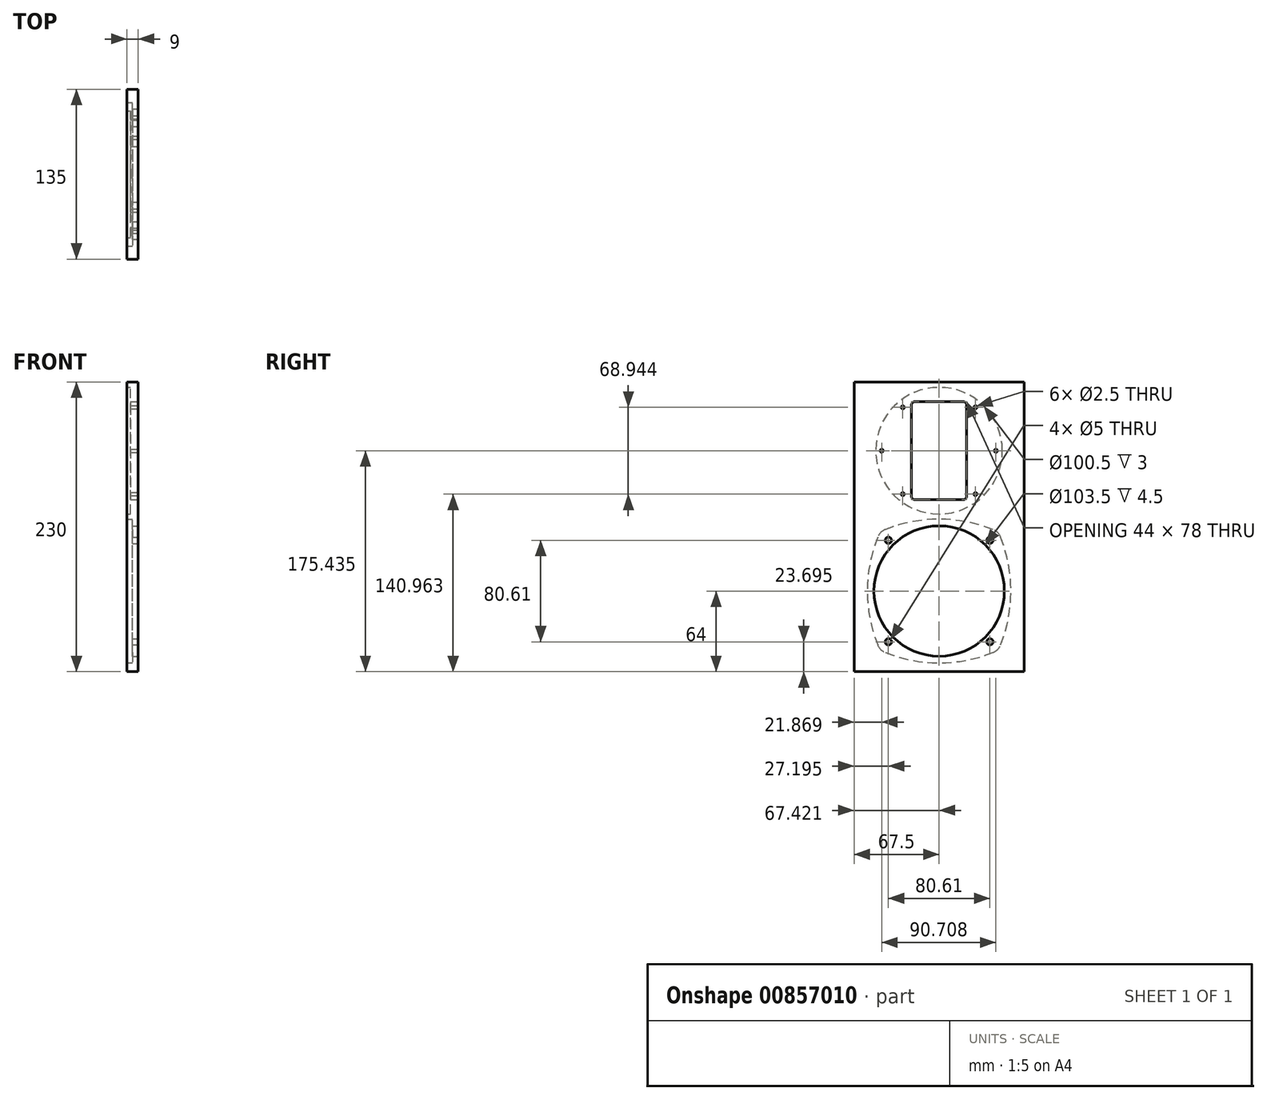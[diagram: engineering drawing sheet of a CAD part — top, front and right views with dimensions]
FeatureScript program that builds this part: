
annotation { "Feature Type Name" : "Feature", "Feature Type Description" : "" }
export const myFeature = defineFeature(function(context is Context, id is Id, definition is map)
    precondition{}
    {
        {
            var Q0;
            Q0=qCreatedBy(makeId("Right.planeOp"),FACE);
            var sketch = newSketch(context, id + "F0", { "sketchPlane" : qUnion([Q0])});
            skLineSegment(sketch, "E0.bottom", {"start": v(67.5, 115) * mm, "end": v(-67.5, 115) * mm});
            skLineSegment(sketch, "E0.left", {"start": v(67.5, 115) * mm, "end": v(67.5, -115) * mm});
            skLineSegment(sketch, "E0.right", {"start": v(-67.5, 115) * mm, "end": v(-67.5, -115) * mm});
            skLineSegment(sketch, "E1", {"start": v(67.5, -115) * mm, "end": v(-67.5, -115) * mm});
            skPoint(sketch, "E2", {"position": v(0, -51) * mm});
            skCircle(sketch, "E3", {"center": v(0, -51) * mm, "radius": 51.75 * mm});
            skCircle(sketch, "E4", {"center": v(40.3, -10.7) * mm, "radius": 2.5 * mm});
            skPoint(sketch, "E5", {"position": v(46.32, -4.68) * mm});
            skPoint(sketch, "E6", {"position": v(47.02, -3.98) * mm});
            skCircle(sketch, "E7.1.0", {"center": v(-40.3, -10.7) * mm, "radius": 2.5 * mm});
            skPoint(sketch, "E7.1.1", {"position": v(-46.32, -4.68) * mm});
            skPoint(sketch, "E7.1.2", {"position": v(-47.02, -3.98) * mm});
            skCircle(sketch, "E7.2.0", {"center": v(-40.3, -91.3) * mm, "radius": 2.5 * mm});
            skPoint(sketch, "E7.2.1", {"position": v(-46.32, -97.32) * mm});
            skPoint(sketch, "E7.2.2", {"position": v(-47.02, -98.02) * mm});
            skCircle(sketch, "E7.3.0", {"center": v(40.3, -91.3) * mm, "radius": 2.5 * mm});
            skPoint(sketch, "E7.3.1", {"position": v(46.32, -97.32) * mm});
            skPoint(sketch, "E7.3.2", {"position": v(47.02, -98.02) * mm});
            skPoint(sketch, "E8.1.0", {"position": v(-57, -51) * mm});
            skPoint(sketch, "E8.2.0", {"position": v(0, -108) * mm});
            skPoint(sketch, "E8.3.0", {"position": v(57, -51) * mm});
            skArc(sketch, "E9", {"start": v(47.02, -3.98) * mm, "mid": v(0, 6) * mm, "end": v(-47.02, -3.98) * mm});
            skArc(sketch, "E10", {"start": v(-47.02, -3.98) * mm, "mid": v(-57, -51) * mm, "end": v(-47.02, -98.02) * mm});
            skArc(sketch, "E11", {"start": v(-47.02, -98.02) * mm, "mid": v(0, -108) * mm, "end": v(47.02, -98.02) * mm});
            skArc(sketch, "E12", {"start": v(47.02, -98.02) * mm, "mid": v(57, -51) * mm, "end": v(47.02, -3.98) * mm});
            skLineSegment(sketch, "E13.trimOffspring", {"start": v(0, 6) * mm, "end": v(0, 115) * mm});
            skLineSegment(sketch, "E14.trimOffspring", {"start": v(46.32, -4.68) * mm, "end": v(47.02, -3.98) * mm});
            skPoint(sketch, "E15.start.orphan", {"position": v(0, -115) * mm});
            skCircle(sketch, "E16", {"center": v(-0.08, 60.44) * mm, "radius": 50.25 * mm});
            skCircle(sketch, "E17.3.0", {"center": v(28.85, 25.96) * mm, "radius": 1.25 * mm});
            skPoint(sketch, "E18", {"position": v(-193.88, 39.27) * mm});
            skLineSegment(sketch, "E19.bottom", {"start": v(-19.08, 99.44) * mm, "end": v(18.92, 99.44) * mm});
            skLineSegment(sketch, "E19.top", {"start": v(-19.08, 21.44) * mm, "end": v(18.92, 21.44) * mm});
            skLineSegment(sketch, "E19.left", {"start": v(-22.08, 96.44) * mm, "end": v(-22.08, 24.44) * mm});
            skLineSegment(sketch, "E19.right", {"start": v(21.92, 96.44) * mm, "end": v(21.92, 24.44) * mm});
            skPoint(sketch, "E20.visualSharp", {"position": v(21.92, 99.44) * mm});
            skArc(sketch, "E20.filletArc", {"start": v(21.92, 96.44) * mm, "mid": v(21.04, 98.56) * mm, "end": v(18.92, 99.44) * mm});
            skPoint(sketch, "E21.visualSharp", {"position": v(-22.08, 99.44) * mm});
            skArc(sketch, "E21.filletArc", {"start": v(-19.08, 99.44) * mm, "mid": v(-21.2, 98.56) * mm, "end": v(-22.08, 96.44) * mm});
            skPoint(sketch, "E22.visualSharp", {"position": v(-22.08, 21.44) * mm});
            skArc(sketch, "E22.filletArc", {"start": v(-22.08, 24.44) * mm, "mid": v(-21.2, 22.31) * mm, "end": v(-19.08, 21.44) * mm});
            skPoint(sketch, "E23.visualSharp", {"position": v(21.92, 21.44) * mm});
            skArc(sketch, "E23.filletArc", {"start": v(18.92, 21.44) * mm, "mid": v(21.04, 22.31) * mm, "end": v(21.92, 24.44) * mm});
            skLineSegment(sketch, "E24", {"start": v(-0.08, 60.44) * mm, "end": v(0, 60.44) * mm});
            skPoint(sketch, "E24.endSnap0", {"position": v(21.92, 60.44) * mm});
            skLineSegment(sketch, "E25", {"start": v(-0.08, 60.44) * mm, "end": v(0, 60.51) * mm});
            skLineSegment(sketch, "E26", {"start": v(-0.08, 60.44) * mm, "end": v(0, 60.34) * mm});
            skCircle(sketch, "E27.MirrorC", {"center": v(-28.85, 25.96) * mm, "radius": 1.25 * mm});
            skCircle(sketch, "E28.MirrorC", {"center": v(-28.85, 94.9) * mm, "radius": 1.25 * mm});
            skCircle(sketch, "E29.MirrorC", {"center": v(28.85, 94.9) * mm, "radius": 1.25 * mm});
            skCircle(sketch, "E30.3.0", {"center": v(45.08, 60.37) * mm, "radius": 1.25 * mm});
            skCircle(sketch, "E31.3.0", {"center": v(-45.63, 60.37) * mm, "radius": 1.25 * mm});
            skPoint(sketch, "E32.trimOffspring.end.orphan", {"position": v(44.92, 60.44) * mm});
            skSolve(sketch);
        }
        {
            var Q0;
            {var subQ4=sQuery(id+"F0.wireOp",EDGE,"E0.left");Q0=makeQuery(id+"F0.imprint","IMPRINT",FACE,{"disambiguationData":[TD([[makeQuery(id+"F0.imprint","IMPRINT",EDGE,{"derivedFrom":subQ4}),-1.0]])]});}
            extrude(context, id + "F1", {"entities" : qUnion([Q0]), "oppositeDirection" : true, "depth" : 9 * mm, "offsetDistance" : 25 * mm});
        }
        {
            var Q0;
            Q0=makeQuery(id+"F0.imprint","IMPRINT",FACE,{"disambiguationData":[TD([[makeQuery(id+"F0.imprint","IMPRINT",EDGE,{"derivedFrom":sQuery(id+"F0.wireOp",EDGE,"E3")}),-1.0]])]});
            extrude(context, id + "F2", {"entities" : qUnion([Q0]), "operationType" : NewBodyOperationType.ADD, "oppositeDirection" : true, "depth" : 4.5 * mm, "offsetDistance" : 25 * mm});
        }
        {
            var Q0;
            Q0=makeQuery(id+"F1.opExtrude","SWEPT_EDGE",EDGE,{"disambiguationData":[OSD([sQuery(id+"F0.wireOp",EDGE,"ZpgzB6W4-esGr-Y8vB-Hv0B-G3QVkJXGVfF8"),sQuery(id+"F0.wireOp",EDGE,"E9"),sQuery(id+"F0.wireOp",EDGE,"E12")])]});
            var Q1;
            Q1=makeQuery(id+"F1.opExtrude","SWEPT_EDGE",EDGE,{"disambiguationData":[OSD([sQuery(id+"F0.wireOp",EDGE,"E9"),sQuery(id+"F0.wireOp",EDGE,"E10")])]});
            var Q2;
            Q2=makeQuery(id+"F1.opExtrude","SWEPT_EDGE",EDGE,{"disambiguationData":[OSD([sQuery(id+"F0.wireOp",EDGE,"E10"),sQuery(id+"F0.wireOp",EDGE,"E11")])]});
            var Q3;
            Q3=makeQuery(id+"F1.opExtrude","SWEPT_EDGE",EDGE,{"disambiguationData":[OSD([sQuery(id+"F0.wireOp",EDGE,"E11"),sQuery(id+"F0.wireOp",EDGE,"E12")])]});
            fillet(context, id + "F3", {"entities" : qUnion([Q0, Q1, Q2, Q3]), "radius" : 11 * mm, "tangentPropagation" : true, "allowEdgeOverflow" : false});
        }
        {
            var Q0;
            Q0=makeQuery(id+"F0.imprint","IMPRINT",FACE,{"disambiguationData":[TD([[makeQuery(id+"F0.imprint","IMPRINT",EDGE,{"derivedFrom":sQuery(id+"F0.wireOp",EDGE,"E17.3.0")}),-1.0]])]});
            var Q1;
            Q1=makeQuery(id+"F0.imprint","IMPRINT",FACE,{"disambiguationData":[TD([[makeQuery(id+"F0.imprint","IMPRINT",EDGE,{"derivedFrom":sQuery(id+"F0.wireOp",EDGE,"E19.left")}),-1.0]])]});
            extrude(context, id + "F4", {"entities" : qUnion([Q0, Q1]), "operationType" : NewBodyOperationType.ADD, "oppositeDirection" : true, "depth" : 6 * mm, "offsetDistance" : 25 * mm});
        }
    });
